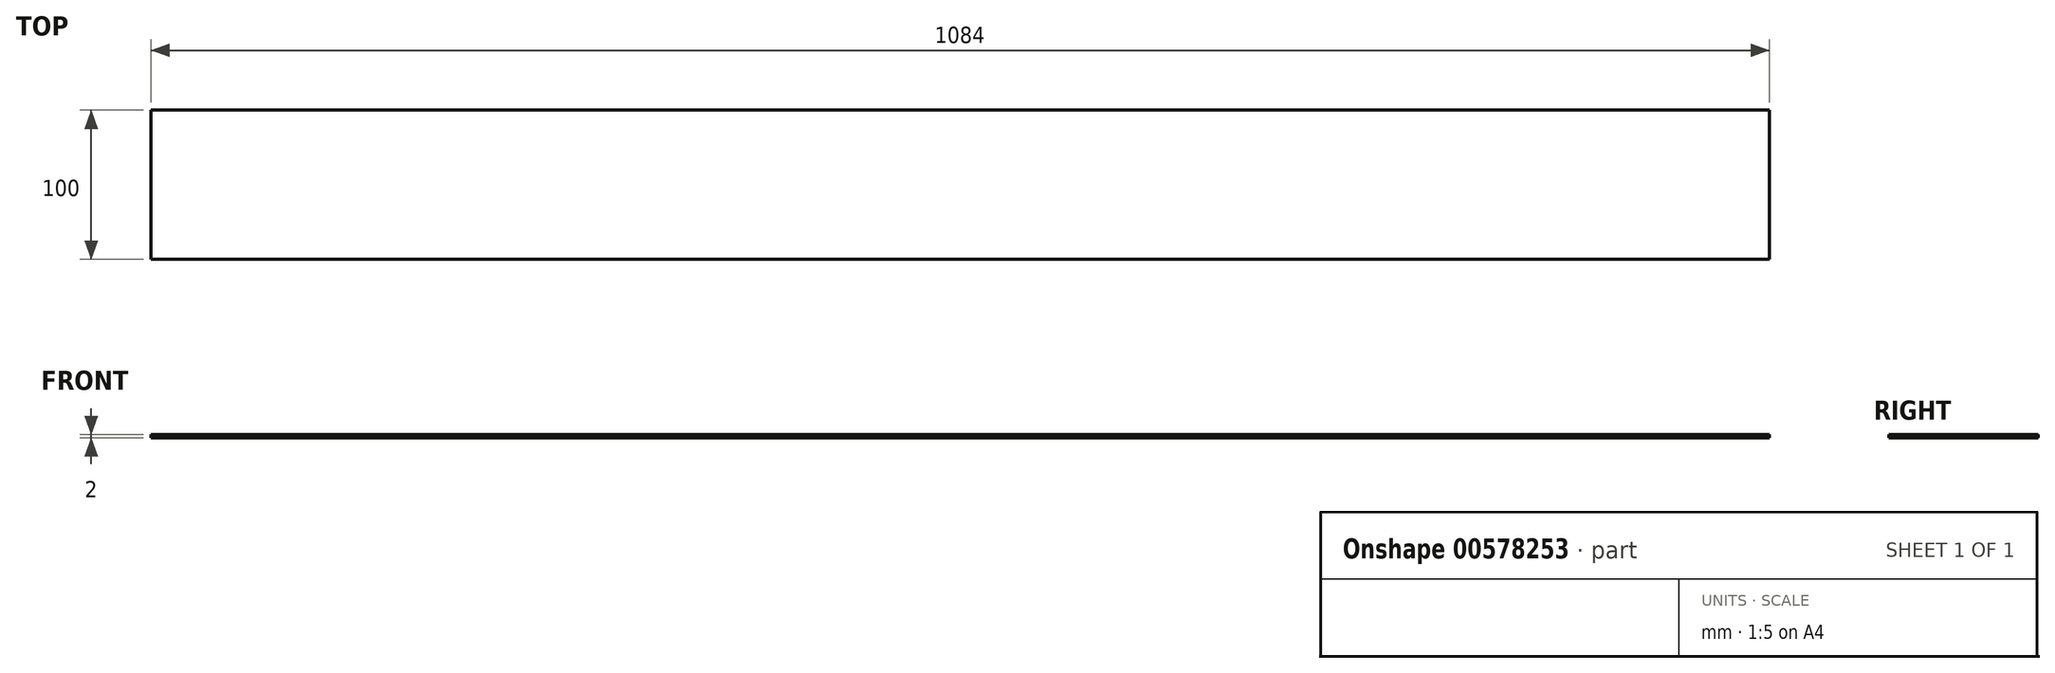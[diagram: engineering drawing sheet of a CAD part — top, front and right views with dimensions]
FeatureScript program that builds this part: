
annotation { "Feature Type Name" : "Feature", "Feature Type Description" : "" }
export const myFeature = defineFeature(function(context is Context, id is Id, definition is map)
    precondition{}
    {
        {
            var Q0;
            Q0=qCreatedBy(makeId("Top.planeOp"),FACE);
            var sketch = newSketch(context, id + "F0", { "sketchPlane" : qUnion([Q0])});
            skLineSegment(sketch, "E0.bottom", {"start": v(542, -50) * mm, "end": v(-542, -50) * mm});
            skLineSegment(sketch, "E0.top", {"start": v(542, 50) * mm, "end": v(-542, 50) * mm});
            skLineSegment(sketch, "E0.left", {"start": v(542, -50) * mm, "end": v(542, 50) * mm});
            skLineSegment(sketch, "E0.right", {"start": v(-542, -50) * mm, "end": v(-542, 50) * mm});
            skPoint(sketch, "E0.middle", {"position": v(0, 0) * mm});
            skSolve(sketch);
        }
        {
            var Q0;
            Q0=makeQuery(id+"F0.imprint","IMPRINT",FACE,{"disambiguationData":[TD([[makeQuery(id+"F0.imprint","IMPRINT",EDGE,{"derivedFrom":sQuery(id+"F0.wireOp",EDGE,"E0.bottom")}),-1.0]])]});
            extrude(context, id + "F1", {"entities" : qUnion([Q0]), "depth" : 2 * mm, "offsetDistance" : 25 * mm});
        }
    });
